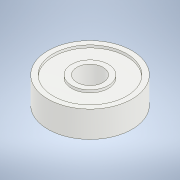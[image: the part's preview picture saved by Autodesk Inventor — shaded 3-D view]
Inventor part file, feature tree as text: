
AUTODESK INVENTOR PART (.ipt)
format: ipt  version: 2022 (Build 260153000, 153)  size: 118,784 bytes
history: imported  units: in
note: dims shown in document units (in); Inventor stores cm internally (conversion verified against a paired STEP export)
features: imported_body x1
ambient origin geometry x8: Origin, YZ Plane, XZ Plane, XY Plane, X Axis, Y Axis, Z Axis, Center Point
bodies: Solid1 (imported_parasolid), Body1 (imported_parasolid)
feature tree (1):
  imported_body  NMx_Import_Brep_tag  [imported B-rep: ~12 faces, bbox_mm=[15.0, 5.0, 0.0]]
